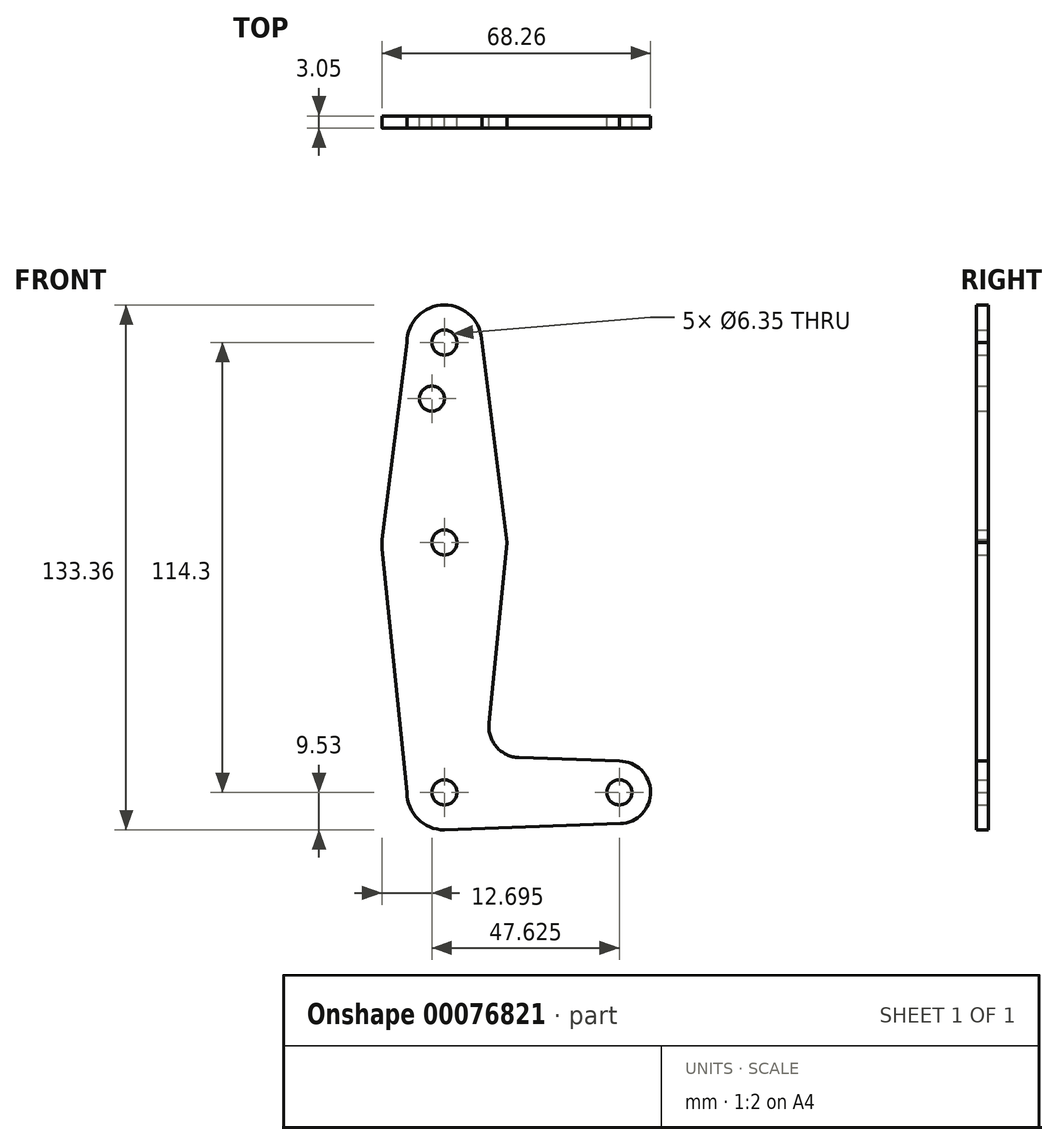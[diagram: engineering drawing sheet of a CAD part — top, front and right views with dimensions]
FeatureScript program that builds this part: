
annotation { "Feature Type Name" : "Feature", "Feature Type Description" : "" }
export const myFeature = defineFeature(function(context is Context, id is Id, definition is map)
    precondition{}
    {
        {
            var Q0;
            Q0=qCreatedBy(makeId("Front.planeOp"),FACE);
            var sketch = newSketch(context, id + "F0", { "sketchPlane" : qUnion([Q0])});
            skLineSegment(sketch, "E0", {"start": v(0, 0) * mm, "end": v(44.45, 0) * mm});
            skCircle(sketch, "E1", {"center": v(0, 114.3) * mm, "radius": 9.53 * mm});
            skCircle(sketch, "E2", {"center": v(0, 63.5) * mm, "radius": 15.88 * mm});
            skCircle(sketch, "E3", {"center": v(0, 0) * mm, "radius": 9.53 * mm});
            skCircle(sketch, "E4", {"center": v(44.45, 0) * mm, "radius": 7.94 * mm});
            skLineSegment(sketch, "E5", {"start": v(0, 0) * mm, "end": v(0, 63.5) * mm});
            skLineSegment(sketch, "E6", {"start": v(0, 63.5) * mm, "end": v(0, 114.3) * mm});
            skLineSegment(sketch, "E7", {"start": v(-9.53, 0) * mm, "end": v(-15.96, 63.5) * mm});
            skLineSegment(sketch, "E8", {"start": v(15.88, 63.5) * mm, "end": v(11.32, 17.58) * mm});
            skLineSegment(sketch, "E9", {"start": v(-9.52, 114.3) * mm, "end": v(-15.96, 63.5) * mm});
            skLineSegment(sketch, "E10", {"start": v(0, -9.52) * mm, "end": v(44.73, -7.93) * mm});
            skLineSegment(sketch, "E11", {"start": v(15.88, 63.5) * mm, "end": v(9.52, 114.3) * mm});
            skLineSegment(sketch, "E12", {"start": v(0, 63.5) * mm, "end": v(0, 100.03) * mm});
            skLineSegment(sketch, "E13", {"start": v(18.94, 8.85) * mm, "end": v(44.45, 7.94) * mm});
            skCircle(sketch, "E14", {"center": v(0, 63.5) * mm, "radius": 3.17 * mm});
            skCircle(sketch, "E15", {"center": v(44.45, 0) * mm, "radius": 3.18 * mm});
            skCircle(sketch, "E16", {"center": v(0, 0) * mm, "radius": 3.18 * mm});
            skCircle(sketch, "E17", {"center": v(0, 114.3) * mm, "radius": 3.18 * mm});
            skCircle(sketch, "E18", {"center": v(-3.18, 100.03) * mm, "radius": 3.18 * mm});
            skPoint(sketch, "E19.newPointB", {"position": v(0, 9.52) * mm});
            skArc(sketch, "E19.filletArc", {"start": v(11.32, 17.58) * mm, "mid": v(13.24, 11.56) * mm, "end": v(18.94, 8.85) * mm});
            skSolve(sketch);
        }
        {
            var Q0;
            {var subQ7=sQuery(id+"F0.wireOp",EDGE,"E18");Q0=makeQuery(id+"F0.imprint","IMPRINT",FACE,{"disambiguationData":[TD([[makeQuery(id+"F0.imprint","IMPRINT",EDGE,{"derivedFrom":subQ7}),-1.0]])]});}
            var Q1;
            {var subQ0=sQuery(id+"F0.wireOp",EDGE,"E11");var subQ1=sQuery(id+"F0.wireOp",EDGE,"E1");var subQ2=makeQuery(id+"F0.imprint","INTERSECT",VERTEX,{"derivedFrom":[subQ1,subQ0]});Q1=makeQuery(id+"F0.imprint","IMPRINT",FACE,{"disambiguationData":[TD([[makeQuery(id+"F0.imprint","IMPRINT",EDGE,{"disambiguationData":[TD([[subQ2,1.0]])],"derivedFrom":subQ1}),-1.0]])]});}
            var Q2;
            Q2=makeQuery(id+"F0.imprint","IMPRINT",FACE,{"disambiguationData":[TD([[makeQuery(id+"F0.imprint","IMPRINT",EDGE,{"derivedFrom":sQuery(id+"F0.wireOp",EDGE,"E17")}),-1.0]])]});
            var Q3;
            {var subQ1=sQuery(id+"F0.wireOp",EDGE,"E2");var subQ6=sQuery(id+"F0.wireOp",EDGE,"E9");var subQ8=makeQuery(id+"F0.imprint","INTERSECT",VERTEX,{"disambiguationData":[OD(0.0)],"derivedFrom":[subQ1,subQ6]});Q3=makeQuery(id+"F0.imprint","IMPRINT",FACE,{"disambiguationData":[TD([[makeQuery(id+"F0.imprint","IMPRINT",EDGE,{"disambiguationData":[TD([[subQ8,1.0]])],"derivedFrom":subQ1}),1.0]])]});}
            var Q4;
            {var subQ1=sQuery(id+"F0.wireOp",EDGE,"E2");var subQ5=sQuery(id+"F0.wireOp",EDGE,"E11");var subQ6=makeQuery(id+"F0.imprint","INTERSECT",VERTEX,{"derivedFrom":[subQ1,subQ5]});Q4=makeQuery(id+"F0.imprint","IMPRINT",FACE,{"disambiguationData":[TD([[makeQuery(id+"F0.imprint","IMPRINT",EDGE,{"disambiguationData":[TD([[subQ6,-1.0]])],"derivedFrom":subQ1}),1.0]])]});}
            var Q5;
            {var subQ0=sQuery(id+"F0.wireOp",EDGE,"E7");var subQ1=sQuery(id+"F0.wireOp",EDGE,"E2");var subQ2=makeQuery(id+"F0.imprint","INTERSECT",VERTEX,{"derivedFrom":[subQ1,subQ0]});Q5=makeQuery(id+"F0.imprint","IMPRINT",FACE,{"disambiguationData":[TD([[makeQuery(id+"F0.imprint","IMPRINT",EDGE,{"disambiguationData":[TD([[subQ2,-1.0]])],"derivedFrom":subQ1}),-1.0]])]});}
            var Q6;
            {var subQ0=sQuery(id+"F0.wireOp",EDGE,"E13");Q6=makeQuery(id+"F0.imprint","IMPRINT",FACE,{"disambiguationData":[TD([[makeQuery(id+"F0.imprint","IMPRINT",EDGE,{"derivedFrom":subQ0}),-1.0]])]});}
            var Q7;
            {var subQ0=sQuery(id+"F0.wireOp",EDGE,"E4");var subQ1=sQuery(id+"F0.wireOp",EDGE,"E0");var subQ2=makeQuery(id+"F0.imprint","INTERSECT",VERTEX,{"derivedFrom":[subQ1,subQ0]});Q7=makeQuery(id+"F0.imprint","IMPRINT",FACE,{"disambiguationData":[TD([[makeQuery(id+"F0.imprint","IMPRINT",EDGE,{"disambiguationData":[TD([[subQ2,1.0]])],"derivedFrom":subQ1}),-1.0]])]});}
            var Q8;
            {var subQ6=sQuery(id+"F0.wireOp",EDGE,"E0");var subQ9=sQuery(id+"F0.wireOp",EDGE,"E16");var subQ10=makeQuery(id+"F0.imprint","INTERSECT",VERTEX,{"derivedFrom":[subQ6,subQ9]});Q8=makeQuery(id+"F0.imprint","IMPRINT",FACE,{"disambiguationData":[TD([[makeQuery(id+"F0.imprint","IMPRINT",EDGE,{"disambiguationData":[TD([[subQ10,-1.0]])],"derivedFrom":subQ6}),-1.0]])]});}
            var Q9;
            {var subQ0=sQuery(id+"F0.wireOp",EDGE,"E16");var subQ1=sQuery(id+"F0.wireOp",EDGE,"E0");var subQ2=makeQuery(id+"F0.imprint","INTERSECT",VERTEX,{"derivedFrom":[subQ1,subQ0]});Q9=makeQuery(id+"F0.imprint","IMPRINT",FACE,{"disambiguationData":[TD([[makeQuery(id+"F0.imprint","IMPRINT",EDGE,{"disambiguationData":[TD([[subQ2,-1.0]])],"derivedFrom":subQ1}),1.0]])]});}
            var Q10;
            Q10=makeQuery(id+"F0.imprint","IMPRINT",FACE,{"disambiguationData":[TD([[makeQuery(id+"F0.imprint","IMPRINT",EDGE,{"derivedFrom":sQuery(id+"F0.wireOp",EDGE,"E15")}),-1.0]])]});
            extrude(context, id + "F1", {"entities" : qUnion([Q0, Q1, Q2, Q3, Q4, Q5, Q6, Q7, Q8, Q9, Q10]), "depth" : 3.05 * mm});
        }
    });
